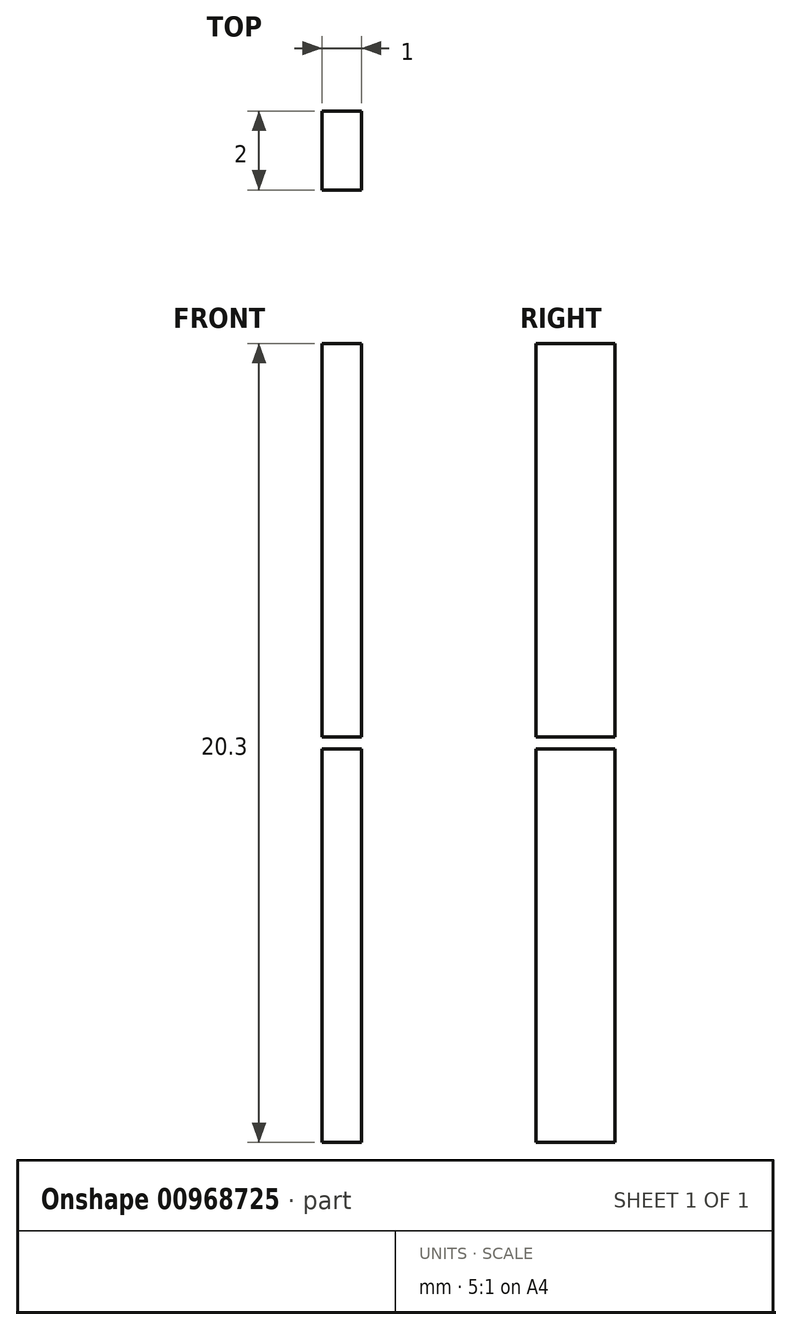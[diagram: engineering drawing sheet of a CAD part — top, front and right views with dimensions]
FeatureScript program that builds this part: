
annotation { "Feature Type Name" : "Feature", "Feature Type Description" : "" }
export const myFeature = defineFeature(function(context is Context, id is Id, definition is map)
    precondition{}
    {
        {
            var Q0;
            Q0=qCreatedBy(makeId("Front.planeOp"),FACE);
            var sketch = newSketch(context, id + "F0", { "sketchPlane" : qUnion([Q0])});
            skLineSegment(sketch, "E0.bottom", {"start": v(-1, 10.15) * mm, "end": v(0, 10.15) * mm});
            skLineSegment(sketch, "E0.top", {"start": v(-1, 0.15) * mm, "end": v(0, 0.15) * mm});
            skLineSegment(sketch, "E0.left", {"start": v(-1, 10.15) * mm, "end": v(-1, 0.15) * mm});
            skLineSegment(sketch, "E0.right", {"start": v(0, 10.15) * mm, "end": v(0, 0.15) * mm});
            skLineSegment(sketch, "E1", {"start": v(0, 0.15) * mm, "end": v(0, 0) * mm, "construction": true});
            skLineSegment(sketch, "E2.MirrorCS", {"start": v(0, -0.15) * mm, "end": v(0, 0) * mm, "construction": true});
            skLineSegment(sketch, "E3.MirrorCS", {"start": v(-1, -0.15) * mm, "end": v(0, -0.15) * mm});
            skLineSegment(sketch, "E4.MirrorCS", {"start": v(0, -10.15) * mm, "end": v(0, -0.15) * mm});
            skLineSegment(sketch, "E5.MirrorCS", {"start": v(-1, -10.15) * mm, "end": v(-1, -0.15) * mm});
            skLineSegment(sketch, "E6.MirrorCS", {"start": v(-1, -10.15) * mm, "end": v(0, -10.15) * mm});
            skSolve(sketch);
        }
        {
            var Q0;
            Q0 = qSketchRegion(id + "F0", true);
            extrude(context, id + "F1", {"entities" : qUnion([Q0]), "depth" : 2 * mm, "offsetDistance" : 25 * mm});
        }
    });
